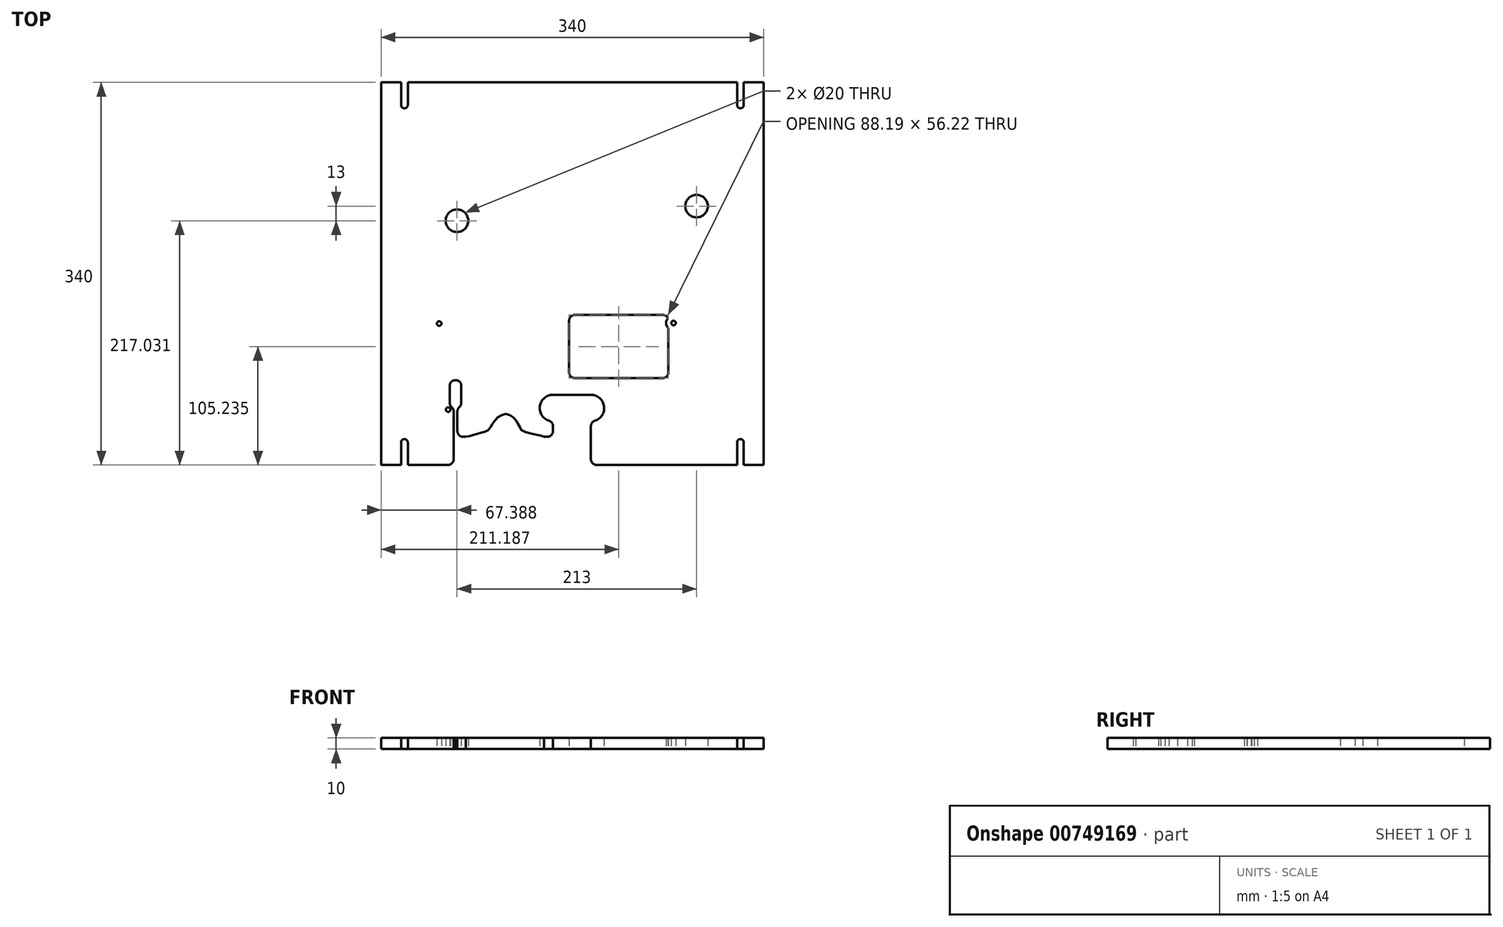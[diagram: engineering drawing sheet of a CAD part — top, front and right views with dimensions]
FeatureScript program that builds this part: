
annotation { "Feature Type Name" : "Feature", "Feature Type Description" : "" }
export const myFeature = defineFeature(function(context is Context, id is Id, definition is map)
    precondition{}
    {
        {
            var Q0;
            Q0=qCreatedBy(makeId("Top.planeOp"),FACE);
            var sketch = newSketch(context, id + "F0", { "sketchPlane" : qUnion([Q0])});
            skCircle(sketch, "E0", {"center": v(-38.58, 92.22) * mm, "radius": 2 * mm});
            skCircle(sketch, "E1", {"center": v(-30.58, 15.72) * mm, "radius": 2 * mm});
            skCircle(sketch, "E2", {"center": v(169.82, 92.72) * mm, "radius": 2 * mm});
            skLineSegment(sketch, "E3.top", {"start": v(62.6, 28.89) * mm, "end": v(96.34, 28.89) * mm});
            skLineSegment(sketch, "E3.left", {"start": v(62.6, -3.44) * mm, "end": v(62.6, 1.08) * mm});
            skLineSegment(sketch, "E3.right", {"start": v(96.34, -3.44) * mm, "end": v(96.34, 1.08) * mm});
            skArc(sketch, "E4", {"start": v(62.6, 28.89) * mm, "mid": v(50.95, 18.88) * mm, "end": v(59.1, 5.86) * mm});
            skArc(sketch, "E5", {"start": v(96.34, 28.89) * mm, "mid": v(108, 18.88) * mm, "end": v(99.85, 5.86) * mm});
            skFitSpline(sketch, "E6", {"points": [v(-14.85, -8.44) * mm, v(-11.17, -7.6) * mm, v(-9.43, -6.99) * mm, v(-7.54, -6.51) * mm, v(-6.07, -6.14) * mm, v(-2.36, -5.2) * mm, v(1.42, -4.2) * mm, v(3.54, -3.53) * mm, v(5.36, -2.23) * mm, v(6.89, -0.19) * mm, v(8.14, 2.14) * mm, v(8.76, 3.1) * mm, v(9.92, 4.88) * mm, v(13.64, 9.16) * mm, v(16.7, 10.86) * mm, v(20.3, 11.88) * mm, v(24.09, 10.94) * mm, v(26.51, 9.42) * mm, v(28.5, 7.43) * mm, v(30.54, 4.79) * mm, v(31.54, 3.05) * mm, v(32.58, 1.1) * mm, v(33.57, -1.06) * mm, v(34.92, -3.01) * mm, v(40.03, -4.66) * mm, v(44.62, -5.79) * mm, v(49.3, -6.74) * mm, v(53.7, -7.93) * mm, v(54.62, -8.44) * mm], "startDerivative": vector(72.5, 26.3) * mm, "endDerivative": vector(29.22, -24.45) * mm});
            skLineSegment(sketch, "E7.trimOffspring", {"start": v(54.62, -8.44) * mm, "end": v(57.6, -8.44) * mm});
            skLineSegment(sketch, "E8", {"start": v(-25.74, -3.44) * mm, "end": v(-25.74, 14.2) * mm});
            skLineSegment(sketch, "E9", {"start": v(-22.38, -3.44) * mm, "end": v(-22.38, 14.2) * mm});
            skLineSegment(sketch, "E10.trimOffspring", {"start": v(-17.38, -8.44) * mm, "end": v(-14.85, -8.44) * mm});
            skArc(sketch, "E11", {"start": v(-29.12, 21.27) * mm, "mid": v(-28.67, 19.48) * mm, "end": v(-27.53, 18.03) * mm});
            skArc(sketch, "E12", {"start": v(-20.58, 18.03) * mm, "mid": v(-19.44, 19.48) * mm, "end": v(-19, 21.27) * mm});
            skArc(sketch, "E13", {"start": v(-24.66, 41.73) * mm, "mid": v(-27.77, 40.55) * mm, "end": v(-29.12, 37.5) * mm});
            skArc(sketch, "E14", {"start": v(-19, 37.5) * mm, "mid": v(-20.34, 40.56) * mm, "end": v(-23.47, 41.73) * mm});
            skLineSegment(sketch, "E15", {"start": v(-24.66, 41.73) * mm, "end": v(-23.47, 41.73) * mm});
            skLineSegment(sketch, "E16", {"start": v(-19, 37.5) * mm, "end": v(-19, 21.27) * mm});
            skLineSegment(sketch, "E17", {"start": v(-29.12, 37.5) * mm, "end": v(-29.12, 21.27) * mm});
            skLineSegment(sketch, "E18.bottom", {"start": v(81.97, 99.9) * mm, "end": v(160.16, 99.9) * mm});
            skLineSegment(sketch, "E18.top", {"start": v(81.97, 43.69) * mm, "end": v(160.16, 43.69) * mm});
            skLineSegment(sketch, "E18.left", {"start": v(76.97, 94.9) * mm, "end": v(76.97, 48.69) * mm});
            skLineSegment(sketch, "E18.right", {"start": v(165.16, 88.01) * mm, "end": v(165.16, 48.69) * mm});
            skPoint(sketch, "E19.visualSharp", {"position": v(76.97, 99.9) * mm});
            skArc(sketch, "E19.filletArc", {"start": v(81.97, 99.9) * mm, "mid": v(78.44, 98.44) * mm, "end": v(76.97, 94.9) * mm});
            skPoint(sketch, "E20.visualSharp", {"position": v(165.16, 99.9) * mm});
            skArc(sketch, "E20.filletArc", {"start": v(164.72, 96.95) * mm, "mid": v(162.88, 99.1) * mm, "end": v(160.16, 99.9) * mm});
            skPoint(sketch, "E21.visualSharp", {"position": v(165.16, 43.69) * mm});
            skArc(sketch, "E21.filletArc", {"start": v(160.16, 43.69) * mm, "mid": v(163.7, 45.15) * mm, "end": v(165.16, 48.69) * mm});
            skPoint(sketch, "E22.visualSharp", {"position": v(76.97, 43.69) * mm});
            skArc(sketch, "E22.filletArc", {"start": v(76.97, 48.69) * mm, "mid": v(78.44, 45.15) * mm, "end": v(81.97, 43.69) * mm});
            skArc(sketch, "E23", {"start": v(165.16, 88.01) * mm, "mid": v(163.2, 92.4) * mm, "end": v(164.72, 96.95) * mm});
            skCircle(sketch, "E24", {"center": v(-22.73, 183.6) * mm, "radius": 10 * mm});
            skCircle(sketch, "E25", {"center": v(190.27, 196.6) * mm, "radius": 10 * mm});
            skArc(sketch, "E26.filletArc", {"start": v(-22.38, -3.44) * mm, "mid": v(-20.91, -6.98) * mm, "end": v(-17.38, -8.44) * mm});
            skPoint(sketch, "E27.visualSharp", {"position": v(-22.38, 17.13) * mm});
            skArc(sketch, "E27.filletArc", {"start": v(-20.58, 18.03) * mm, "mid": v(-21.9, 16.3) * mm, "end": v(-22.38, 14.2) * mm});
            skPoint(sketch, "E28.visualSharp", {"position": v(-25.74, 17.13) * mm});
            skArc(sketch, "E28.filletArc", {"start": v(-25.74, 14.2) * mm, "mid": v(-26.2, 16.3) * mm, "end": v(-27.53, 18.03) * mm});
            skPoint(sketch, "E29.visualSharp", {"position": v(62.6, 5.32) * mm});
            skArc(sketch, "E29.filletArc", {"start": v(62.6, 1.08) * mm, "mid": v(61.63, 4.05) * mm, "end": v(59.1, 5.86) * mm});
            skPoint(sketch, "E30.visualSharp", {"position": v(62.6, -8.44) * mm});
            skArc(sketch, "E30.filletArc", {"start": v(57.6, -8.44) * mm, "mid": v(61.14, -6.98) * mm, "end": v(62.6, -3.44) * mm});
            skPoint(sketch, "E31.visualSharp", {"position": v(96.34, 5.32) * mm});
            skArc(sketch, "E31.filletArc", {"start": v(99.85, 5.86) * mm, "mid": v(97.31, 4.05) * mm, "end": v(96.34, 1.08) * mm});
            skLineSegment(sketch, "E32.bottom", {"start": v(223.74, -15) * mm, "end": v(-64.12, -15) * mm, "construction": true});
            skLineSegment(sketch, "E32.top", {"start": v(223.74, 217.6) * mm, "end": v(-64.12, 217.6) * mm, "construction": true});
            skLineSegment(sketch, "E32.left", {"start": v(223.74, -15) * mm, "end": v(223.74, 217.6) * mm, "construction": true});
            skLineSegment(sketch, "E32.right", {"start": v(-64.12, -15) * mm, "end": v(-64.12, 217.6) * mm, "construction": true});
            skPoint(sketch, "E32.middle", {"position": v(79.81, 101.3) * mm});
            skPoint(sketch, "E33.middle", {"position": v(223.74, 6.56) * mm});
            skLineSegment(sketch, "E34", {"start": v(-90.12, 306.56) * mm, "end": v(249.88, 306.56) * mm});
            skLineSegment(sketch, "E35", {"start": v(79.88, 306.56) * mm, "end": v(79.88, -178.47) * mm, "construction": true});
            skLineSegment(sketch, "E36", {"start": v(96.34, -3.44) * mm, "end": v(96.34, -28.44) * mm});
            skLineSegment(sketch, "E37", {"start": v(101.34, -33.44) * mm, "end": v(249.88, -33.44) * mm});
            skLineSegment(sketch, "E38", {"start": v(-90.12, -33.44) * mm, "end": v(-30.74, -33.44) * mm});
            skLineSegment(sketch, "E39", {"start": v(-25.74, -28.44) * mm, "end": v(-25.74, -3.44) * mm});
            skLineSegment(sketch, "E40", {"start": v(-90.12, 306.56) * mm, "end": v(-90.12, -33.44) * mm});
            skLineSegment(sketch, "E41", {"start": v(249.88, 306.56) * mm, "end": v(249.88, -33.44) * mm});
            skLineSegment(sketch, "E42", {"start": v(-90.12, 136.56) * mm, "end": v(249.88, 136.56) * mm, "construction": true});
            skPoint(sketch, "E43.visualSharp", {"position": v(-25.74, -33.44) * mm});
            skArc(sketch, "E43.filletArc", {"start": v(-30.74, -33.44) * mm, "mid": v(-27.2, -31.98) * mm, "end": v(-25.74, -28.44) * mm});
            skPoint(sketch, "E44.visualSharp", {"position": v(96.34, -33.44) * mm});
            skArc(sketch, "E44.filletArc", {"start": v(96.34, -28.44) * mm, "mid": v(97.8, -31.98) * mm, "end": v(101.34, -33.44) * mm});
            skArc(sketch, "E45", {"start": v(226.24, 286.56) * mm, "mid": v(229.24, 283.56) * mm, "end": v(232.24, 286.56) * mm});
            skLineSegment(sketch, "E46", {"start": v(226.24, 286.56) * mm, "end": v(226.24, 306.56) * mm});
            skLineSegment(sketch, "E47", {"start": v(232.24, 286.56) * mm, "end": v(232.24, 306.56) * mm});
            skLineSegment(sketch, "E48.MirrorCS", {"start": v(-66.48, 286.56) * mm, "end": v(-66.48, 306.56) * mm});
            skLineSegment(sketch, "E49.MirrorCS", {"start": v(-72.48, 286.56) * mm, "end": v(-72.48, 306.56) * mm});
            skArc(sketch, "E50.MirrorCS", {"start": v(-66.48, 286.56) * mm, "mid": v(-69.48, 283.56) * mm, "end": v(-72.48, 286.56) * mm});
            skLineSegment(sketch, "E51.MirrorCS", {"start": v(-72.48, -13.44) * mm, "end": v(-72.48, -33.44) * mm});
            skLineSegment(sketch, "E52.MirrorCS", {"start": v(-66.48, -13.44) * mm, "end": v(-66.48, -33.44) * mm});
            skArc(sketch, "E53.MirrorCS", {"start": v(-66.48, -13.44) * mm, "mid": v(-69.48, -10.44) * mm, "end": v(-72.48, -13.44) * mm});
            skLineSegment(sketch, "E54.MirrorCS", {"start": v(226.24, -13.44) * mm, "end": v(226.24, -33.44) * mm});
            skArc(sketch, "E55.MirrorCS", {"start": v(226.24, -13.44) * mm, "mid": v(229.24, -10.44) * mm, "end": v(232.24, -13.44) * mm});
            skLineSegment(sketch, "E56.MirrorCS", {"start": v(232.24, -13.44) * mm, "end": v(232.24, -33.44) * mm});
            skSolve(sketch);
        }
        {
            var Q0;
            Q0=makeQuery(id+"F0.imprint","IMPRINT",FACE,{"disambiguationData":[TD([[makeQuery(id+"F0.imprint","IMPRINT",EDGE,{"derivedFrom":sQuery(id+"F0.wireOp",EDGE,"E0")}),-1.0]])]});
            extrude(context, id + "F1", {"entities" : qUnion([Q0]), "depth" : 10 * mm, "offsetDistance" : 25 * mm});
        }
    });
